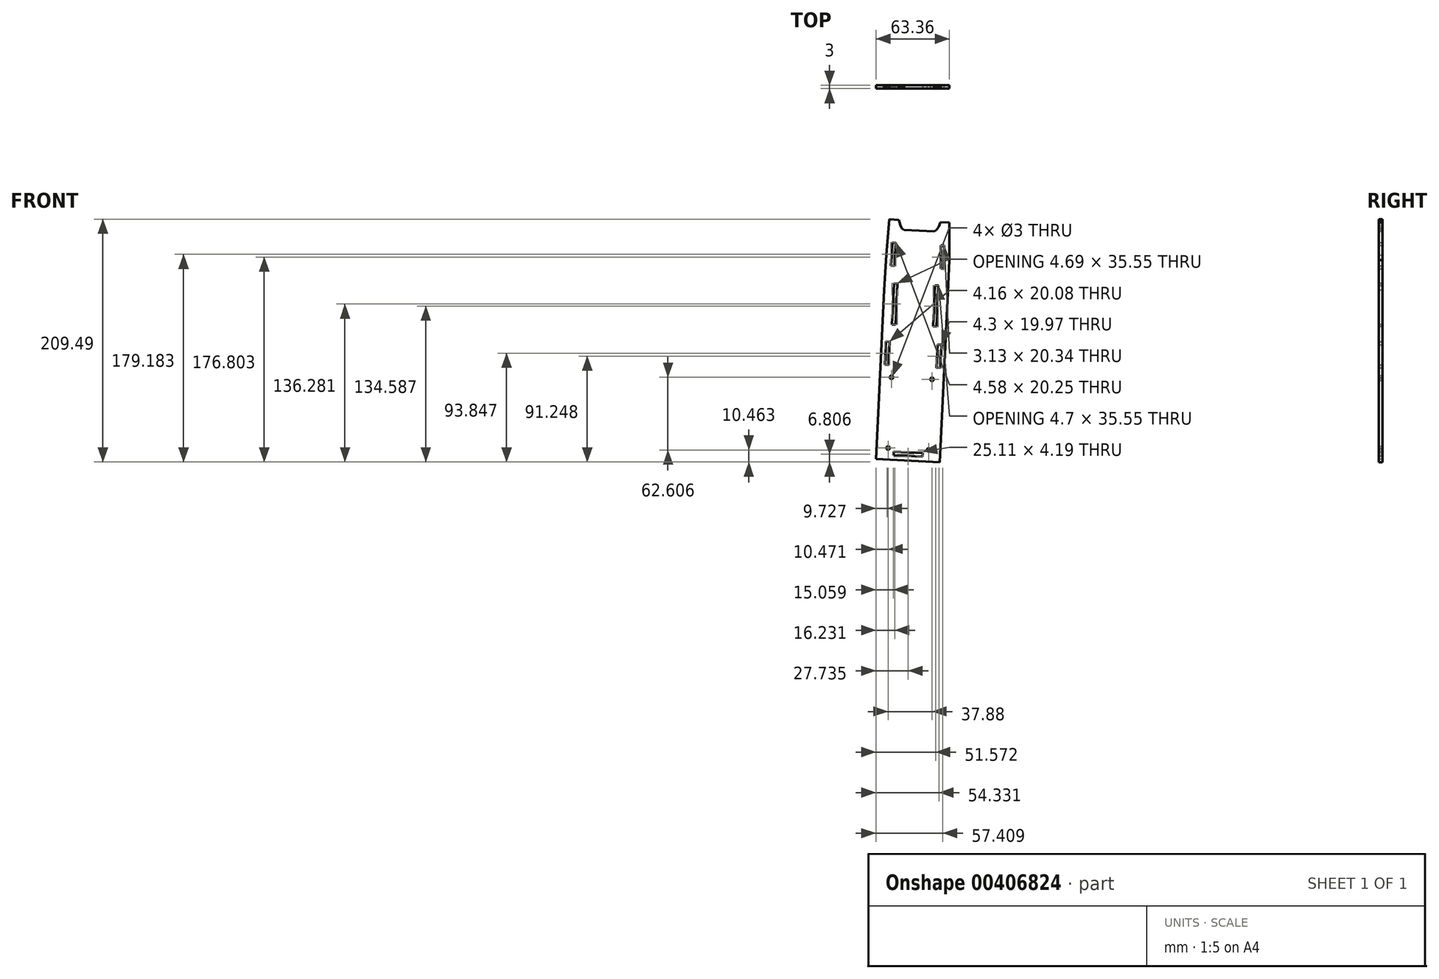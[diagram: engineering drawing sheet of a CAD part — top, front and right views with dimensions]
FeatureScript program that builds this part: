
annotation { "Feature Type Name" : "Feature", "Feature Type Description" : "" }
export const myFeature = defineFeature(function(context is Context, id is Id, definition is map)
    precondition{}
    {
        {
            var Q0;
            Q0=qCreatedBy(makeId("Front.planeOp"),FACE);
            var sketch = newSketch(context, id + "F0", { "sketchPlane" : qUnion([Q0])});
            skLineSegment(sketch, "E0", {"start": v(5.53, -158.37) * mm, "end": v(60.46, -161) * mm});
            skLineSegment(sketch, "E1", {"start": v(60.46, -161) * mm, "end": v(64.58, -75.1) * mm});
            skLineSegment(sketch, "E2", {"start": v(5.53, -158.37) * mm, "end": v(9.64, -72.47) * mm});
            skLineSegment(sketch, "E3", {"start": v(10.3, -136.97) * mm, "end": v(13.5, -137.12) * mm});
            skLineSegment(sketch, "E4", {"start": v(13.5, -137.12) * mm, "end": v(14.46, -117.2) * mm});
            skLineSegment(sketch, "E5", {"start": v(14.46, -117.2) * mm, "end": v(11.25, -117.04) * mm});
            skLineSegment(sketch, "E6", {"start": v(11.25, -117.04) * mm, "end": v(10.3, -136.97) * mm});
            skLineSegment(sketch, "E7", {"start": v(58.2, -139.6) * mm, "end": v(59.13, -119.86) * mm});
            skLineSegment(sketch, "E8", {"start": v(59.13, -119.86) * mm, "end": v(55.77, -119.7) * mm});
            skLineSegment(sketch, "E9", {"start": v(55.77, -119.7) * mm, "end": v(54.83, -139.66) * mm});
            skLineSegment(sketch, "E10", {"start": v(54.83, -139.66) * mm, "end": v(58.2, -139.6) * mm});
            skLineSegment(sketch, "E11", {"start": v(9.64, -72.47) * mm, "end": v(11.5, -42.48) * mm});
            skLineSegment(sketch, "E12", {"start": v(11.5, -42.48) * mm, "end": v(14.14, -11.44) * mm});
            skLineSegment(sketch, "E13", {"start": v(14.14, -11.44) * mm, "end": v(22.57, -12.12) * mm});
            skLineSegment(sketch, "E14", {"start": v(22.57, -12.12) * mm, "end": v(23.82, -16.67) * mm});
            skLineSegment(sketch, "E15", {"start": v(23.82, -16.67) * mm, "end": v(25.08, -19.48) * mm});
            skLineSegment(sketch, "E16", {"start": v(25.08, -19.48) * mm, "end": v(27.02, -20.83) * mm});
            skLineSegment(sketch, "E17", {"start": v(27.02, -20.83) * mm, "end": v(52.75, -22.11) * mm});
            skLineSegment(sketch, "E18", {"start": v(52.75, -22.11) * mm, "end": v(54.85, -20.83) * mm});
            skLineSegment(sketch, "E19", {"start": v(54.85, -20.83) * mm, "end": v(56.77, -18.18) * mm});
            skLineSegment(sketch, "E20", {"start": v(56.77, -18.18) * mm, "end": v(58.23, -14.07) * mm});
            skLineSegment(sketch, "E21", {"start": v(58.23, -14.07) * mm, "end": v(66.01, -14.44) * mm});
            skLineSegment(sketch, "E22", {"start": v(66.01, -14.44) * mm, "end": v(66.01, -46.88) * mm});
            skLineSegment(sketch, "E23", {"start": v(66.01, -46.88) * mm, "end": v(64.58, -75.1) * mm});
            skLineSegment(sketch, "E24", {"start": v(15.42, -51.64) * mm, "end": v(18.5, -51.87) * mm});
            skLineSegment(sketch, "E25", {"start": v(18.5, -51.87) * mm, "end": v(20, -31.86) * mm});
            skLineSegment(sketch, "E26", {"start": v(20, -31.86) * mm, "end": v(16.9, -31.62) * mm});
            skLineSegment(sketch, "E27", {"start": v(16.9, -31.62) * mm, "end": v(15.42, -51.64) * mm});
            skLineSegment(sketch, "E28", {"start": v(58.5, -33.96) * mm, "end": v(58.5, -54.06) * mm});
            skLineSegment(sketch, "E29", {"start": v(58.5, -54.06) * mm, "end": v(61.62, -54.3) * mm});
            skLineSegment(sketch, "E30", {"start": v(61.62, -54.3) * mm, "end": v(61.62, -34.2) * mm});
            skLineSegment(sketch, "E31", {"start": v(61.62, -34.2) * mm, "end": v(58.5, -33.96) * mm});
            skSolve(sketch);
        }
        {
            var Q0;
            Q0 = qSketchRegion(id + "F0", true);
            extrude(context, id + "F1", {"entities" : qUnion([Q0]), "depth" : 3 * mm});
        }
        {
            var Q0;
            Q0=makeQuery(id+"F1.opExtrude","SWEPT_FACE",FACE,{"disambiguationData":[OSD([sQuery(id+"F0.wireOp",EDGE,"E0")])]});
            var sketch = newSketch(context, id + "F2", { "sketchPlane" : qUnion([Q0])});
            skLineSegment(sketch, "E32.bottom", {"start": v(13.1, 3) * mm, "end": v(68.1, 3) * mm});
            skLineSegment(sketch, "E32.top", {"start": v(13.1, 0) * mm, "end": v(68.1, 0) * mm});
            skLineSegment(sketch, "E32.left", {"start": v(13.1, 3) * mm, "end": v(13.1, 0) * mm});
            skLineSegment(sketch, "E32.right", {"start": v(68.1, 3) * mm, "end": v(68.1, 0) * mm});
            skSolve(sketch);
        }
        {
            var Q0;
            Q0 = qSketchRegion(id + "F2", true);
            extrude(context, id + "F3", {"entities" : qUnion([Q0]), "operationType" : NewBodyOperationType.ADD, "depth" : 60 * mm});
        }
        {
            var Q0;
            Q0=makeQuery(id+"F3.boolean.opBoolean","MERGE",FACE,{"derivedFrom":[makeQuery(id+"F1.opExtrude","CAP_FACE",FACE,{"disambiguationData":[OSD([sQuery(id+"F0.wireOp",EDGE,"E0"),sQuery(id+"F0.wireOp",EDGE,"E1"),sQuery(id+"F0.wireOp",EDGE,"E2"),sQuery(id+"F0.wireOp",EDGE,"E3"),sQuery(id+"F0.wireOp",EDGE,"E4"),sQuery(id+"F0.wireOp",EDGE,"E5"),sQuery(id+"F0.wireOp",EDGE,"E6"),sQuery(id+"F0.wireOp",EDGE,"E7"),sQuery(id+"F0.wireOp",EDGE,"E8"),sQuery(id+"F0.wireOp",EDGE,"E9"),sQuery(id+"F0.wireOp",EDGE,"E10"),sQuery(id+"F0.wireOp",EDGE,"E11"),sQuery(id+"F0.wireOp",EDGE,"E12"),sQuery(id+"F0.wireOp",EDGE,"E13"),sQuery(id+"F0.wireOp",EDGE,"E14"),sQuery(id+"F0.wireOp",EDGE,"E15"),sQuery(id+"F0.wireOp",EDGE,"E16"),sQuery(id+"F0.wireOp",EDGE,"E17"),sQuery(id+"F0.wireOp",EDGE,"E18"),sQuery(id+"F0.wireOp",EDGE,"E19"),sQuery(id+"F0.wireOp",EDGE,"E20"),sQuery(id+"F0.wireOp",EDGE,"E21"),sQuery(id+"F0.wireOp",EDGE,"E22"),sQuery(id+"F0.wireOp",EDGE,"E23"),sQuery(id+"F0.wireOp",EDGE,"E24"),sQuery(id+"F0.wireOp",EDGE,"E25"),sQuery(id+"F0.wireOp",EDGE,"E26"),sQuery(id+"F0.wireOp",EDGE,"E27"),sQuery(id+"F0.wireOp",EDGE,"E28"),sQuery(id+"F0.wireOp",EDGE,"E29"),sQuery(id+"F0.wireOp",EDGE,"E30"),sQuery(id+"F0.wireOp",EDGE,"E31")])],"isStart":false}),makeQuery(id+"F3.opExtrude","SWEPT_FACE",FACE,{"disambiguationData":[OSD([sQuery(id+"F2.wireOp",EDGE,"E32.bottom")])]})]});
            var sketch = newSketch(context, id + "F4", { "sketchPlane" : qUnion([Q0])});
            skLineSegment(sketch, "E33", {"start": v(16.88, -95.02) * mm, "end": v(16.53, -102.28) * mm});
            skLineSegment(sketch, "E34", {"start": v(19.53, -102.42) * mm, "end": v(21.23, -67.02) * mm});
            skLineSegment(sketch, "E35", {"start": v(16.88, -95.02) * mm, "end": v(18.22, -67.02) * mm});
            skLineSegment(sketch, "E36", {"start": v(21.23, -67.02) * mm, "end": v(18.22, -66.88) * mm});
            skLineSegment(sketch, "E37", {"start": v(18.22, -66.88) * mm, "end": v(18.22, -67.02) * mm});
            skLineSegment(sketch, "E38", {"start": v(16.53, -102.28) * mm, "end": v(19.53, -102.42) * mm});
            skLineSegment(sketch, "E39", {"start": v(30.12, -219.62) * mm, "end": v(38.16, -51.84) * mm, "construction": true});
            skLineSegment(sketch, "E40.MirrorCS", {"start": v(51.87, -103.97) * mm, "end": v(53.57, -68.57) * mm});
            skLineSegment(sketch, "E41.MirrorCS", {"start": v(55.22, -96.86) * mm, "end": v(56.56, -68.86) * mm});
            skLineSegment(sketch, "E42.MirrorCS", {"start": v(55.22, -96.86) * mm, "end": v(54.87, -104.12) * mm});
            skLineSegment(sketch, "E43.MirrorCS", {"start": v(54.87, -104.12) * mm, "end": v(51.87, -103.97) * mm});
            skLineSegment(sketch, "E44.MirrorCS", {"start": v(53.57, -68.57) * mm, "end": v(56.57, -68.71) * mm});
            skLineSegment(sketch, "E45", {"start": v(56.56, -68.86) * mm, "end": v(56.57, -68.71) * mm});
            skSolve(sketch);
        }
        {
            var Q0;
            Q0 = qSketchRegion(id + "F4", true);
            extrude(context, id + "F5", {"entities" : qUnion([Q0]), "operationType" : NewBodyOperationType.REMOVE, "endBound" : BoundingType.THROUGH_ALL, "oppositeDirection" : true, "depth" : 25 * mm});
        }
        {
            var Q0;
            Q0=makeQuery(id+"F3.boolean.opBoolean","MERGE",FACE,{"derivedFrom":[makeQuery(id+"F1.opExtrude","CAP_FACE",FACE,{"disambiguationData":[OSD([sQuery(id+"F0.wireOp",EDGE,"E0"),sQuery(id+"F0.wireOp",EDGE,"E1"),sQuery(id+"F0.wireOp",EDGE,"E2"),sQuery(id+"F0.wireOp",EDGE,"E3"),sQuery(id+"F0.wireOp",EDGE,"E4"),sQuery(id+"F0.wireOp",EDGE,"E5"),sQuery(id+"F0.wireOp",EDGE,"E6"),sQuery(id+"F0.wireOp",EDGE,"E7"),sQuery(id+"F0.wireOp",EDGE,"E8"),sQuery(id+"F0.wireOp",EDGE,"E9"),sQuery(id+"F0.wireOp",EDGE,"E10"),sQuery(id+"F0.wireOp",EDGE,"E11"),sQuery(id+"F0.wireOp",EDGE,"E12"),sQuery(id+"F0.wireOp",EDGE,"E13"),sQuery(id+"F0.wireOp",EDGE,"E14"),sQuery(id+"F0.wireOp",EDGE,"E15"),sQuery(id+"F0.wireOp",EDGE,"E16"),sQuery(id+"F0.wireOp",EDGE,"E17"),sQuery(id+"F0.wireOp",EDGE,"E18"),sQuery(id+"F0.wireOp",EDGE,"E19"),sQuery(id+"F0.wireOp",EDGE,"E20"),sQuery(id+"F0.wireOp",EDGE,"E21"),sQuery(id+"F0.wireOp",EDGE,"E22"),sQuery(id+"F0.wireOp",EDGE,"E23"),sQuery(id+"F0.wireOp",EDGE,"E24"),sQuery(id+"F0.wireOp",EDGE,"E25"),sQuery(id+"F0.wireOp",EDGE,"E26"),sQuery(id+"F0.wireOp",EDGE,"E27"),sQuery(id+"F0.wireOp",EDGE,"E28"),sQuery(id+"F0.wireOp",EDGE,"E29"),sQuery(id+"F0.wireOp",EDGE,"E30"),sQuery(id+"F0.wireOp",EDGE,"E31")])],"isStart":false}),makeQuery(id+"F3.opExtrude","SWEPT_FACE",FACE,{"disambiguationData":[OSD([sQuery(id+"F2.wireOp",EDGE,"E32.bottom")])]})]});
            var sketch = newSketch(context, id + "F6", { "sketchPlane" : qUnion([Q0])});
            skLineSegment(sketch, "E46", {"start": v(13.12, -208.8) * mm, "end": v(48.08, -210.47) * mm, "construction": true});
            skLineSegment(sketch, "E47", {"start": v(48.08, -210.47) * mm, "end": v(51, -149.54) * mm, "construction": true});
            skLineSegment(sketch, "E48", {"start": v(51, -149.54) * mm, "end": v(16.04, -147.86) * mm, "construction": true});
            skLineSegment(sketch, "E49", {"start": v(16.04, -147.86) * mm, "end": v(13.12, -208.8) * mm, "construction": true});
            skLineSegment(sketch, "E50", {"start": v(30.12, -219.62) * mm, "end": v(34.7, -124.23) * mm, "construction": true});
            skPoint(sketch, "E51", {"position": v(30.6, -209.63) * mm});
            skCircle(sketch, "E52", {"center": v(16.04, -147.86) * mm, "radius": 1.5 * mm});
            skCircle(sketch, "E53", {"center": v(51, -149.54) * mm, "radius": 1.5 * mm});
            skCircle(sketch, "E54", {"center": v(13.12, -208.8) * mm, "radius": 1.5 * mm});
            skCircle(sketch, "E55", {"center": v(48.08, -210.47) * mm, "radius": 1.5 * mm});
            skLineSegment(sketch, "E56", {"start": v(42.8, -216.22) * mm, "end": v(17.83, -215.02) * mm});
            skLineSegment(sketch, "E57", {"start": v(17.83, -215.02) * mm, "end": v(17.97, -212.03) * mm});
            skLineSegment(sketch, "E58", {"start": v(17.97, -212.03) * mm, "end": v(42.94, -213.22) * mm});
            skLineSegment(sketch, "E59", {"start": v(42.94, -213.22) * mm, "end": v(42.8, -216.22) * mm});
            skPoint(sketch, "E60", {"position": v(30.31, -215.62) * mm});
            skSolve(sketch);
        }
        {
            var Q0;
            Q0 = qSketchRegion(id + "F6", true);
            extrude(context, id + "F7", {"entities" : qUnion([Q0]), "operationType" : NewBodyOperationType.REMOVE, "oppositeDirection" : true, "depth" : 25 * mm});
        }
    });
